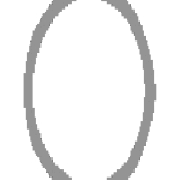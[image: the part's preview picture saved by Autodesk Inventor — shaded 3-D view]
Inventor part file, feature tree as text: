
AUTODESK INVENTOR PART (.ipt)
format: ipt  version: 2021 (Build 250183000, 183)  size: 115,200 bytes
history: native  units: in
note: dims shown in document units (in); Inventor stores cm internally (conversion verified against a paired STEP export)
features: other x4, sketch x3, plane x1
ambient origin geometry x8: Origin, YZ Plane, XZ Plane, XY Plane, X Axis, Y Axis, Z Axis, Center Point
bodies: Solid1 (feature_tree), Body (feature_tree)
feature tree (8):
  other  "Driven Length"
  other  "Frame Generator"
  other  "Start Plane"
  other  "End Plane"
  sketch  "Sketch"  dims[d2=1.3416in d4=-0.0in d5=1.3416in d6=0.12in d7=0.0in d8=90.0deg d9=1.3416in]
  sketch  "Sketch2"  dims[d0=1.0in]
  plane  "Work Plane3"
  sketch  "Sketch3"  dims[d1=0.065in]
